annotation { "Feature Type Name" : "Feature", "Feature Type Description" : "" }
export const myFeature = defineFeature(function(context is Context, id is Id, definition is map)
    precondition{}
    {
        {
            var Q0;
            Q0=qCreatedBy(makeId("Top.planeOp"),FACE);
            var sketch = newSketch(context, id + "F0", { "sketchPlane" : qUnion([Q0])});
            skCircle(sketch, "E0", {"center": v(0, 0) * mm, "radius": 8 * mm});
            skCircle(sketch, "E1", {"center": v(0, 0) * mm, "radius": 12.5 * mm});
            skLineSegment(sketch, "E2", {"start": v(-35, 12.5) * mm, "end": v(0, 12.5) * mm});
            skLineSegment(sketch, "E3", {"start": v(-35, -12.5) * mm, "end": v(0, -12.5) * mm});
            skLineSegment(sketch, "E4", {"start": v(-35, 12.5) * mm, "end": v(-120.23, 12.5) * mm, "construction": true});
            skLineSegment(sketch, "E5", {"start": v(-35, -12.5) * mm, "end": v(-116.04, -12.5) * mm, "construction": true});
            skLineSegment(sketch, "E6", {"start": v(-35, 12.5) * mm, "end": v(-116.39, 2.5) * mm});
            skLineSegment(sketch, "E7", {"start": v(-35, -12.5) * mm, "end": v(-116.39, -2.5) * mm});
            skLineSegment(sketch, "E8", {"start": v(-116.39, -2.5) * mm, "end": v(-116.39, 2.5) * mm});
            skSolve(sketch);
        }
        {
            var Q0;
            {var subQ1=sQuery(id+"F0.wireOp",EDGE,"E2");Q0=makeQuery(id+"F0.imprint","IMPRINT",FACE,{"disambiguationData":[TD([[makeQuery(id+"F0.imprint","IMPRINT",EDGE,{"derivedFrom":subQ1}),-1.0]])]});}
            var Q1;
            Q1=makeQuery(id+"F0.imprint","IMPRINT",FACE,{"disambiguationData":[TD([[makeQuery(id+"F0.imprint","IMPRINT",EDGE,{"derivedFrom":sQuery(id+"F0.wireOp",EDGE,"E0")}),-1.0]])]});
            extrude(context, id + "F1", {"entities" : qUnion([Q0, Q1]), "depth" : 3.5 * mm});
        }
        {
            var Q0;
            Q0=makeQuery(id+"F1.opExtrude","CAP_FACE",FACE,{"disambiguationData":[OSD([sQuery(id+"F0.wireOp",EDGE,"E0"),sQuery(id+"F0.wireOp",EDGE,"E1"),sQuery(id+"F0.wireOp",EDGE,"E2"),sQuery(id+"F0.wireOp",EDGE,"E3"),sQuery(id+"F0.wireOp",EDGE,"E6"),sQuery(id+"F0.wireOp",EDGE,"E7"),sQuery(id+"F0.wireOp",EDGE,"E8")])],"isStart":false});
            var sketch = newSketch(context, id + "F2", { "sketchPlane" : qUnion([Q0])});
            skCircle(sketch, "E9", {"center": v(0, 0) * mm, "radius": 12.5 * mm});
            skCircle(sketch, "E10", {"center": v(0, 0) * mm, "radius": 8 * mm});
            skSolve(sketch);
        }
        {
            var Q0;
            Q0=makeQuery(id+"F2.imprint","IMPRINT",FACE,{"disambiguationData":[TD([[makeQuery(id+"F2.imprint","IMPRINT",EDGE,{"derivedFrom":sQuery(id+"F2.wireOp",EDGE,"E10")}),-1.0]])]});
            extrude(context, id + "F3", {"entities" : qUnion([Q0]), "operationType" : NewBodyOperationType.ADD, "depth" : 2 * mm});
        }
        {
            var Q0;
            Q0=makeQuery(id+"F3.opExtrude","CAP_FACE",FACE,{"disambiguationData":[OSD([sQuery(id+"F2.wireOp",EDGE,"E9"),sQuery(id+"F2.wireOp",EDGE,"E10")])],"isStart":false});
            var sketch = newSketch(context, id + "F4", { "sketchPlane" : qUnion([Q0])});
            skLineSegment(sketch, "E11.bottom", {"start": v(-0.75, 11.75) * mm, "end": v(0.75, 11.75) * mm});
            skLineSegment(sketch, "E11.top", {"start": v(-0.75, 8.75) * mm, "end": v(0.75, 8.75) * mm});
            skLineSegment(sketch, "E11.left", {"start": v(-0.75, 11.75) * mm, "end": v(-0.75, 8.75) * mm});
            skLineSegment(sketch, "E11.right", {"start": v(0.75, 11.75) * mm, "end": v(0.75, 8.75) * mm});
            skLineSegment(sketch, "E12.1.0", {"start": v(3.26, 11.31) * mm, "end": v(2.61, 8.38) * mm});
            skLineSegment(sketch, "E12.1.1", {"start": v(1.15, 8.7) * mm, "end": v(2.61, 8.38) * mm});
            skLineSegment(sketch, "E12.1.2", {"start": v(1.8, 11.64) * mm, "end": v(1.15, 8.7) * mm});
            skLineSegment(sketch, "E12.1.3", {"start": v(1.8, 11.64) * mm, "end": v(3.26, 11.31) * mm});
            skLineSegment(sketch, "E12.2.0", {"start": v(5.61, 10.35) * mm, "end": v(4.35, 7.63) * mm});
            skLineSegment(sketch, "E12.2.1", {"start": v(3, 8.26) * mm, "end": v(4.35, 7.63) * mm});
            skLineSegment(sketch, "E12.2.2", {"start": v(4.25, 10.98) * mm, "end": v(3, 8.26) * mm});
            skLineSegment(sketch, "E12.2.3", {"start": v(4.25, 10.98) * mm, "end": v(5.61, 10.35) * mm});
            skLineSegment(sketch, "E12.3.0", {"start": v(7.7, 8.9) * mm, "end": v(5.9, 6.51) * mm});
            skLineSegment(sketch, "E12.3.1", {"start": v(4.7, 7.42) * mm, "end": v(5.9, 6.51) * mm});
            skLineSegment(sketch, "E12.3.2", {"start": v(6.51, 9.8) * mm, "end": v(4.7, 7.42) * mm});
            skLineSegment(sketch, "E12.3.3", {"start": v(6.51, 9.8) * mm, "end": v(7.7, 8.9) * mm});
            skLineSegment(sketch, "E12.4.0", {"start": v(9.44, 7.04) * mm, "end": v(7.15, 5.1) * mm});
            skLineSegment(sketch, "E12.4.1", {"start": v(6.18, 6.24) * mm, "end": v(7.15, 5.1) * mm});
            skLineSegment(sketch, "E12.4.2", {"start": v(8.47, 8.18) * mm, "end": v(6.18, 6.24) * mm});
            skLineSegment(sketch, "E12.4.3", {"start": v(8.47, 8.18) * mm, "end": v(9.44, 7.04) * mm});
            skLineSegment(sketch, "E12.5.0", {"start": v(10.73, 4.84) * mm, "end": v(8.08, 3.44) * mm});
            skLineSegment(sketch, "E12.5.1", {"start": v(7.38, 4.76) * mm, "end": v(8.08, 3.44) * mm});
            skLineSegment(sketch, "E12.5.2", {"start": v(10.03, 6.17) * mm, "end": v(7.38, 4.76) * mm});
            skLineSegment(sketch, "E12.5.3", {"start": v(10.03, 6.17) * mm, "end": v(10.73, 4.84) * mm});
            skLineSegment(sketch, "E12.6.0", {"start": v(11.52, 2.42) * mm, "end": v(8.63, 1.62) * mm});
            skLineSegment(sketch, "E12.6.1", {"start": v(8.23, 3.06) * mm, "end": v(8.63, 1.62) * mm});
            skLineSegment(sketch, "E12.6.2", {"start": v(11.12, 3.87) * mm, "end": v(8.23, 3.06) * mm});
            skLineSegment(sketch, "E12.6.3", {"start": v(11.12, 3.87) * mm, "end": v(11.52, 2.42) * mm});
            skLineSegment(sketch, "E12.7.0", {"start": v(11.77, -0.11) * mm, "end": v(8.78, -0.28) * mm});
            skLineSegment(sketch, "E12.7.1", {"start": v(8.7, 1.22) * mm, "end": v(8.78, -0.28) * mm});
            skLineSegment(sketch, "E12.7.2", {"start": v(11.7, 1.39) * mm, "end": v(8.7, 1.22) * mm});
            skLineSegment(sketch, "E12.7.3", {"start": v(11.7, 1.39) * mm, "end": v(11.77, -0.11) * mm});
            skLineSegment(sketch, "E12.8.0", {"start": v(11.47, -2.64) * mm, "end": v(8.51, -2.16) * mm});
            skLineSegment(sketch, "E12.8.1", {"start": v(8.76, -0.68) * mm, "end": v(8.51, -2.16) * mm});
            skLineSegment(sketch, "E12.8.2", {"start": v(11.72, -1.16) * mm, "end": v(8.76, -0.68) * mm});
            skLineSegment(sketch, "E12.8.3", {"start": v(11.72, -1.16) * mm, "end": v(11.47, -2.64) * mm});
            skLineSegment(sketch, "E12.9.0", {"start": v(10.64, -5.05) * mm, "end": v(7.85, -3.94) * mm});
            skLineSegment(sketch, "E12.9.1", {"start": v(8.4, -2.54) * mm, "end": v(7.85, -3.94) * mm});
            skLineSegment(sketch, "E12.9.2", {"start": v(11.2, -3.65) * mm, "end": v(8.4, -2.54) * mm});
            skLineSegment(sketch, "E12.9.3", {"start": v(11.2, -3.65) * mm, "end": v(10.64, -5.05) * mm});
            skLineSegment(sketch, "E12.10.0", {"start": v(9.3, -7.21) * mm, "end": v(6.82, -5.53) * mm});
            skLineSegment(sketch, "E12.10.1", {"start": v(7.66, -4.29) * mm, "end": v(6.82, -5.53) * mm});
            skLineSegment(sketch, "E12.10.2", {"start": v(10.15, -5.97) * mm, "end": v(7.66, -4.29) * mm});
            skLineSegment(sketch, "E12.10.3", {"start": v(10.15, -5.97) * mm, "end": v(9.3, -7.21) * mm});
            skLineSegment(sketch, "E12.11.0", {"start": v(7.54, -9.05) * mm, "end": v(5.47, -6.87) * mm});
            skLineSegment(sketch, "E12.11.1", {"start": v(6.56, -5.84) * mm, "end": v(5.47, -6.87) * mm});
            skLineSegment(sketch, "E12.11.2", {"start": v(8.62, -8.01) * mm, "end": v(6.56, -5.84) * mm});
            skLineSegment(sketch, "E12.11.3", {"start": v(8.62, -8.01) * mm, "end": v(7.54, -9.05) * mm});
            skLineSegment(sketch, "E12.12.0", {"start": v(5.42, -10.45) * mm, "end": v(3.87, -7.88) * mm});
            skLineSegment(sketch, "E12.12.1", {"start": v(5.15, -7.11) * mm, "end": v(3.87, -7.88) * mm});
            skLineSegment(sketch, "E12.12.2", {"start": v(6.7, -9.68) * mm, "end": v(5.15, -7.11) * mm});
            skLineSegment(sketch, "E12.12.3", {"start": v(6.7, -9.68) * mm, "end": v(5.42, -10.45) * mm});
            skLineSegment(sketch, "E12.13.0", {"start": v(3.04, -11.37) * mm, "end": v(2.08, -8.53) * mm});
            skLineSegment(sketch, "E12.13.1", {"start": v(3.5, -8.05) * mm, "end": v(2.08, -8.53) * mm});
            skLineSegment(sketch, "E12.13.2", {"start": v(4.46, -10.9) * mm, "end": v(3.5, -8.05) * mm});
            skLineSegment(sketch, "E12.13.3", {"start": v(4.46, -10.9) * mm, "end": v(3.04, -11.37) * mm});
            skLineSegment(sketch, "E12.14.0", {"start": v(0.52, -11.76) * mm, "end": v(0.2, -8.78) * mm});
            skLineSegment(sketch, "E12.14.1", {"start": v(1.7, -8.62) * mm, "end": v(0.2, -8.78) * mm});
            skLineSegment(sketch, "E12.14.2", {"start": v(2.02, -11.6) * mm, "end": v(1.7, -8.62) * mm});
            skLineSegment(sketch, "E12.14.3", {"start": v(2.02, -11.6) * mm, "end": v(0.52, -11.76) * mm});
            skLineSegment(sketch, "E12.15.0", {"start": v(-2.02, -11.6) * mm, "end": v(-1.7, -8.62) * mm});
            skLineSegment(sketch, "E12.15.1", {"start": v(-0.2, -8.78) * mm, "end": v(-1.7, -8.62) * mm});
            skLineSegment(sketch, "E12.15.2", {"start": v(-0.52, -11.76) * mm, "end": v(-0.2, -8.78) * mm});
            skLineSegment(sketch, "E12.15.3", {"start": v(-0.52, -11.76) * mm, "end": v(-2.02, -11.6) * mm});
            skLineSegment(sketch, "E12.16.0", {"start": v(-4.46, -10.9) * mm, "end": v(-3.5, -8.05) * mm});
            skLineSegment(sketch, "E12.16.1", {"start": v(-2.08, -8.53) * mm, "end": v(-3.5, -8.05) * mm});
            skLineSegment(sketch, "E12.16.2", {"start": v(-3.04, -11.37) * mm, "end": v(-2.08, -8.53) * mm});
            skLineSegment(sketch, "E12.16.3", {"start": v(-3.04, -11.37) * mm, "end": v(-4.46, -10.9) * mm});
            skLineSegment(sketch, "E12.17.0", {"start": v(-6.7, -9.68) * mm, "end": v(-5.15, -7.11) * mm});
            skLineSegment(sketch, "E12.17.1", {"start": v(-3.87, -7.88) * mm, "end": v(-5.15, -7.11) * mm});
            skLineSegment(sketch, "E12.17.2", {"start": v(-5.42, -10.45) * mm, "end": v(-3.87, -7.88) * mm});
            skLineSegment(sketch, "E12.17.3", {"start": v(-5.42, -10.45) * mm, "end": v(-6.7, -9.68) * mm});
            skLineSegment(sketch, "E12.18.0", {"start": v(-8.62, -8.01) * mm, "end": v(-6.56, -5.84) * mm});
            skLineSegment(sketch, "E12.18.1", {"start": v(-5.47, -6.87) * mm, "end": v(-6.56, -5.84) * mm});
            skLineSegment(sketch, "E12.18.2", {"start": v(-7.54, -9.05) * mm, "end": v(-5.47, -6.87) * mm});
            skLineSegment(sketch, "E12.18.3", {"start": v(-7.54, -9.05) * mm, "end": v(-8.62, -8.01) * mm});
            skLineSegment(sketch, "E12.19.0", {"start": v(-10.15, -5.97) * mm, "end": v(-7.66, -4.29) * mm});
            skLineSegment(sketch, "E12.19.1", {"start": v(-6.82, -5.53) * mm, "end": v(-7.66, -4.29) * mm});
            skLineSegment(sketch, "E12.19.2", {"start": v(-9.3, -7.21) * mm, "end": v(-6.82, -5.53) * mm});
            skLineSegment(sketch, "E12.19.3", {"start": v(-9.3, -7.21) * mm, "end": v(-10.15, -5.97) * mm});
            skLineSegment(sketch, "E12.20.0", {"start": v(-11.2, -3.65) * mm, "end": v(-8.4, -2.54) * mm});
            skLineSegment(sketch, "E12.20.1", {"start": v(-7.85, -3.94) * mm, "end": v(-8.4, -2.54) * mm});
            skLineSegment(sketch, "E12.20.2", {"start": v(-10.64, -5.05) * mm, "end": v(-7.85, -3.94) * mm});
            skLineSegment(sketch, "E12.20.3", {"start": v(-10.64, -5.05) * mm, "end": v(-11.2, -3.65) * mm});
            skLineSegment(sketch, "E12.21.0", {"start": v(-11.72, -1.16) * mm, "end": v(-8.76, -0.68) * mm});
            skLineSegment(sketch, "E12.21.1", {"start": v(-8.51, -2.16) * mm, "end": v(-8.76, -0.68) * mm});
            skLineSegment(sketch, "E12.21.2", {"start": v(-11.47, -2.64) * mm, "end": v(-8.51, -2.16) * mm});
            skLineSegment(sketch, "E12.21.3", {"start": v(-11.47, -2.64) * mm, "end": v(-11.72, -1.16) * mm});
            skLineSegment(sketch, "E12.22.0", {"start": v(-11.7, 1.39) * mm, "end": v(-8.7, 1.22) * mm});
            skLineSegment(sketch, "E12.22.1", {"start": v(-8.78, -0.28) * mm, "end": v(-8.7, 1.22) * mm});
            skLineSegment(sketch, "E12.22.2", {"start": v(-11.77, -0.11) * mm, "end": v(-8.78, -0.28) * mm});
            skLineSegment(sketch, "E12.22.3", {"start": v(-11.77, -0.11) * mm, "end": v(-11.7, 1.39) * mm});
            skLineSegment(sketch, "E12.23.0", {"start": v(-11.12, 3.87) * mm, "end": v(-8.23, 3.06) * mm});
            skLineSegment(sketch, "E12.23.1", {"start": v(-8.63, 1.62) * mm, "end": v(-8.23, 3.06) * mm});
            skLineSegment(sketch, "E12.23.2", {"start": v(-11.52, 2.42) * mm, "end": v(-8.63, 1.62) * mm});
            skLineSegment(sketch, "E12.23.3", {"start": v(-11.52, 2.42) * mm, "end": v(-11.12, 3.87) * mm});
            skLineSegment(sketch, "E12.24.0", {"start": v(-10.03, 6.17) * mm, "end": v(-7.38, 4.76) * mm});
            skLineSegment(sketch, "E12.24.1", {"start": v(-8.08, 3.44) * mm, "end": v(-7.38, 4.76) * mm});
            skLineSegment(sketch, "E12.24.2", {"start": v(-10.73, 4.84) * mm, "end": v(-8.08, 3.44) * mm});
            skLineSegment(sketch, "E12.24.3", {"start": v(-10.73, 4.84) * mm, "end": v(-10.03, 6.17) * mm});
            skLineSegment(sketch, "E12.25.0", {"start": v(-8.47, 8.18) * mm, "end": v(-6.18, 6.24) * mm});
            skLineSegment(sketch, "E12.25.1", {"start": v(-7.15, 5.1) * mm, "end": v(-6.18, 6.24) * mm});
            skLineSegment(sketch, "E12.25.2", {"start": v(-9.44, 7.04) * mm, "end": v(-7.15, 5.1) * mm});
            skLineSegment(sketch, "E12.25.3", {"start": v(-9.44, 7.04) * mm, "end": v(-8.47, 8.18) * mm});
            skLineSegment(sketch, "E12.26.0", {"start": v(-6.51, 9.8) * mm, "end": v(-4.7, 7.42) * mm});
            skLineSegment(sketch, "E12.26.1", {"start": v(-5.9, 6.51) * mm, "end": v(-4.7, 7.42) * mm});
            skLineSegment(sketch, "E12.26.2", {"start": v(-7.7, 8.9) * mm, "end": v(-5.9, 6.51) * mm});
            skLineSegment(sketch, "E12.26.3", {"start": v(-7.7, 8.9) * mm, "end": v(-6.51, 9.8) * mm});
            skLineSegment(sketch, "E12.27.0", {"start": v(-4.25, 10.98) * mm, "end": v(-3, 8.26) * mm});
            skLineSegment(sketch, "E12.27.1", {"start": v(-4.35, 7.63) * mm, "end": v(-3, 8.26) * mm});
            skLineSegment(sketch, "E12.27.2", {"start": v(-5.61, 10.35) * mm, "end": v(-4.35, 7.63) * mm});
            skLineSegment(sketch, "E12.27.3", {"start": v(-5.61, 10.35) * mm, "end": v(-4.25, 10.98) * mm});
            skLineSegment(sketch, "E12.28.0", {"start": v(-1.8, 11.64) * mm, "end": v(-1.15, 8.7) * mm});
            skLineSegment(sketch, "E12.28.1", {"start": v(-2.61, 8.38) * mm, "end": v(-1.15, 8.7) * mm});
            skLineSegment(sketch, "E12.28.2", {"start": v(-3.26, 11.31) * mm, "end": v(-2.61, 8.38) * mm});
            skLineSegment(sketch, "E12.28.3", {"start": v(-3.26, 11.31) * mm, "end": v(-1.8, 11.64) * mm});
            skPoint(sketch, "E12.center", {"position": v(0, 0) * mm});
            skLineSegment(sketch, "E12.anchor1", {"start": v(0, 0) * mm, "end": v(0.75, 8.75) * mm, "construction": true});
            skSolve(sketch);
        }
        {
            var Q0;
            Q0 = qSketchRegion(id + "F4", true);
            extrude(context, id + "F5", {"entities" : qUnion([Q0]), "operationType" : NewBodyOperationType.ADD, "depth" : .25 * mm});
        }
        {
            var Q0;
            Q0=makeQuery(id+"F1.opExtrude","CAP_FACE",FACE,{"disambiguationData":[OSD([sQuery(id+"F0.wireOp",EDGE,"E0"),sQuery(id+"F0.wireOp",EDGE,"E1"),sQuery(id+"F0.wireOp",EDGE,"E2"),sQuery(id+"F0.wireOp",EDGE,"E3"),sQuery(id+"F0.wireOp",EDGE,"E6"),sQuery(id+"F0.wireOp",EDGE,"E7"),sQuery(id+"F0.wireOp",EDGE,"E8")])],"isStart":true});
            var sketch = newSketch(context, id + "F6", { "sketchPlane" : qUnion([Q0])});
            skText(sketch, "E13", { "text": "BMS ART", "fontName": "OpenSans-Italic.ttf"});
            const initialGuessF6  = {"E13": [-0.06706, -0.00307, 1, 0, 0.00636]};
            skSetInitialGuess(sketch, initialGuessF6);
            skSolve(sketch);
        }
        {
            var Q0;
            Q0 = qSketchRegion(id + "F6", true);
            extrude(context, id + "F7", {"entities" : qUnion([Q0]), "operationType" : NewBodyOperationType.REMOVE, "oppositeDirection" : true, "depth" : 2 * mm});
        }
        {
            var Q0;
            Q0=qCreatedBy(makeId("Top.planeOp"),FACE);
            var sketch = newSketch(context, id + "F8", { "sketchPlane" : qUnion([Q0])});
            skLineSegment(sketch, "E14.bottom", {"start": v(-116.39, 1) * mm, "end": v(-96.39, 1) * mm});
            skLineSegment(sketch, "E14.top", {"start": v(-116.39, -1) * mm, "end": v(-96.39, -1) * mm});
            skLineSegment(sketch, "E14.left", {"start": v(-116.39, 1) * mm, "end": v(-116.39, -1) * mm});
            skLineSegment(sketch, "E14.right", {"start": v(-96.39, 1) * mm, "end": v(-96.39, -1) * mm});
            skSolve(sketch);
        }
        {
            var Q0;
            Q0 = qSketchRegion(id + "F8", true);
            extrude(context, id + "F9", {"entities" : qUnion([Q0]), "operationType" : NewBodyOperationType.REMOVE, "depth" : 2 * mm});
        }
    });